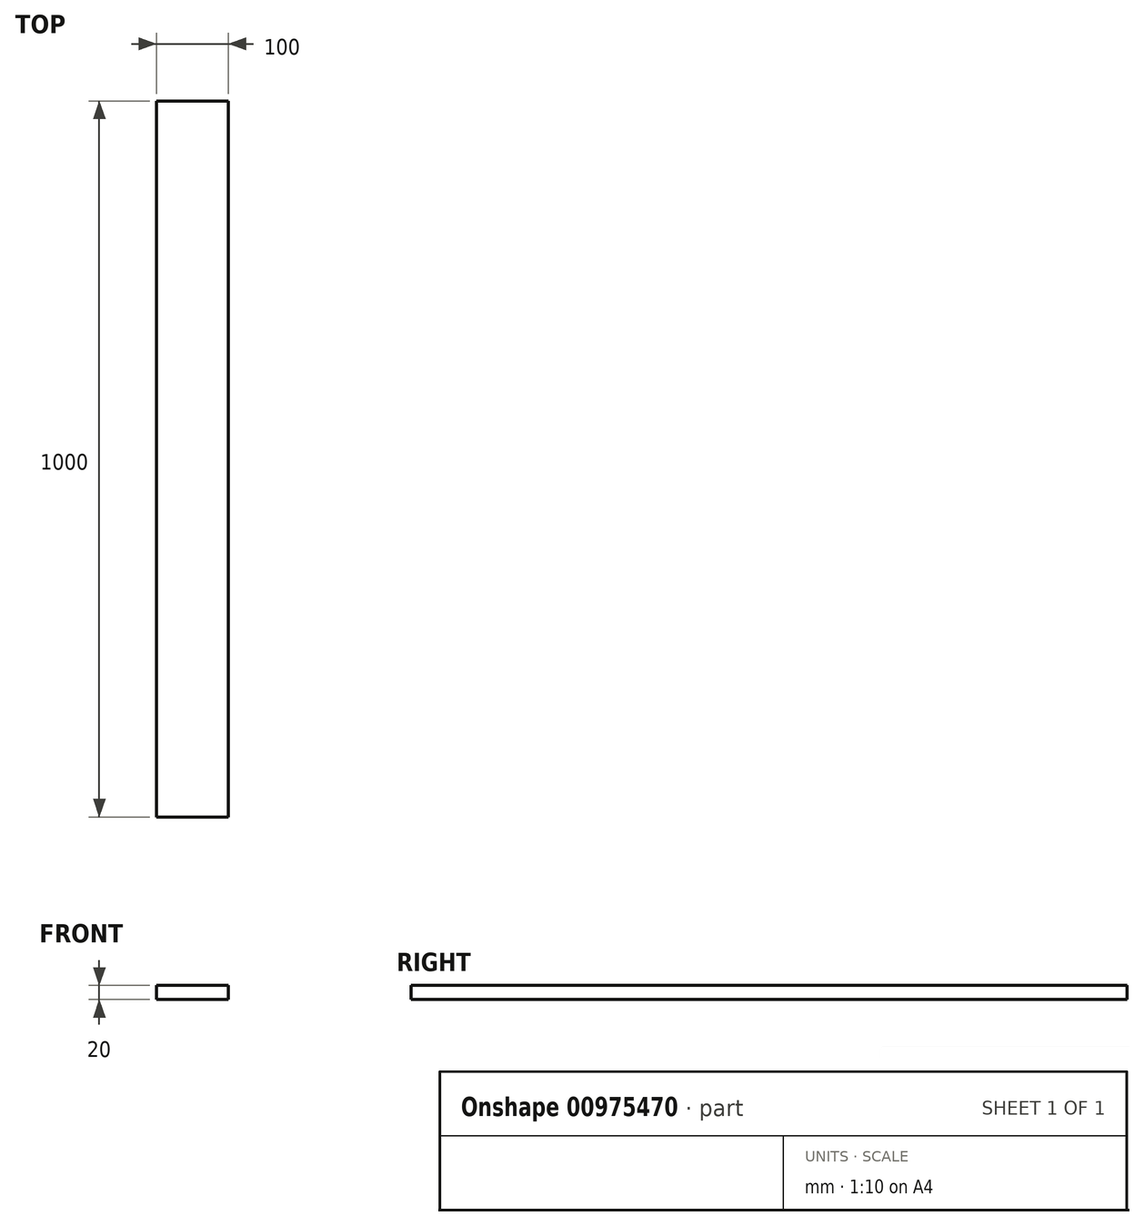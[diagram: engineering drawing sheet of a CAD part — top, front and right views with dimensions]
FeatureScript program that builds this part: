
annotation { "Feature Type Name" : "Feature", "Feature Type Description" : "" }
export const myFeature = defineFeature(function(context is Context, id is Id, definition is map)
    precondition{}
    {
        {
            var Q0;
            Q0=qCreatedBy(makeId("Top.planeOp"),FACE);
            var sketch = newSketch(context, id + "F0", { "sketchPlane" : qUnion([Q0])});
            skLineSegment(sketch, "E0.bottom", {"start": v(-90.6, -176.89) * mm, "end": v(9.4, -176.89) * mm});
            skLineSegment(sketch, "E0.top", {"start": v(-90.6, 823.11) * mm, "end": v(9.4, 823.11) * mm});
            skLineSegment(sketch, "E0.left", {"start": v(-90.6, -176.89) * mm, "end": v(-90.6, 823.11) * mm});
            skLineSegment(sketch, "E0.right", {"start": v(9.4, -176.89) * mm, "end": v(9.4, 823.11) * mm});
            skSolve(sketch);
        }
        {
            var Q0;
            Q0=makeQuery(id+"F0.imprint","IMPRINT",FACE,{"disambiguationData":[TD([[makeQuery(id+"F0.imprint","IMPRINT",EDGE,{"derivedFrom":sQuery(id+"F0.wireOp",EDGE,"E0.bottom")}),1.0]])]});
            extrude(context, id + "F1", {"entities" : qUnion([Q0]), "depth" : 20 * mm, "offsetDistance" : 25 * mm});
        }
    });
